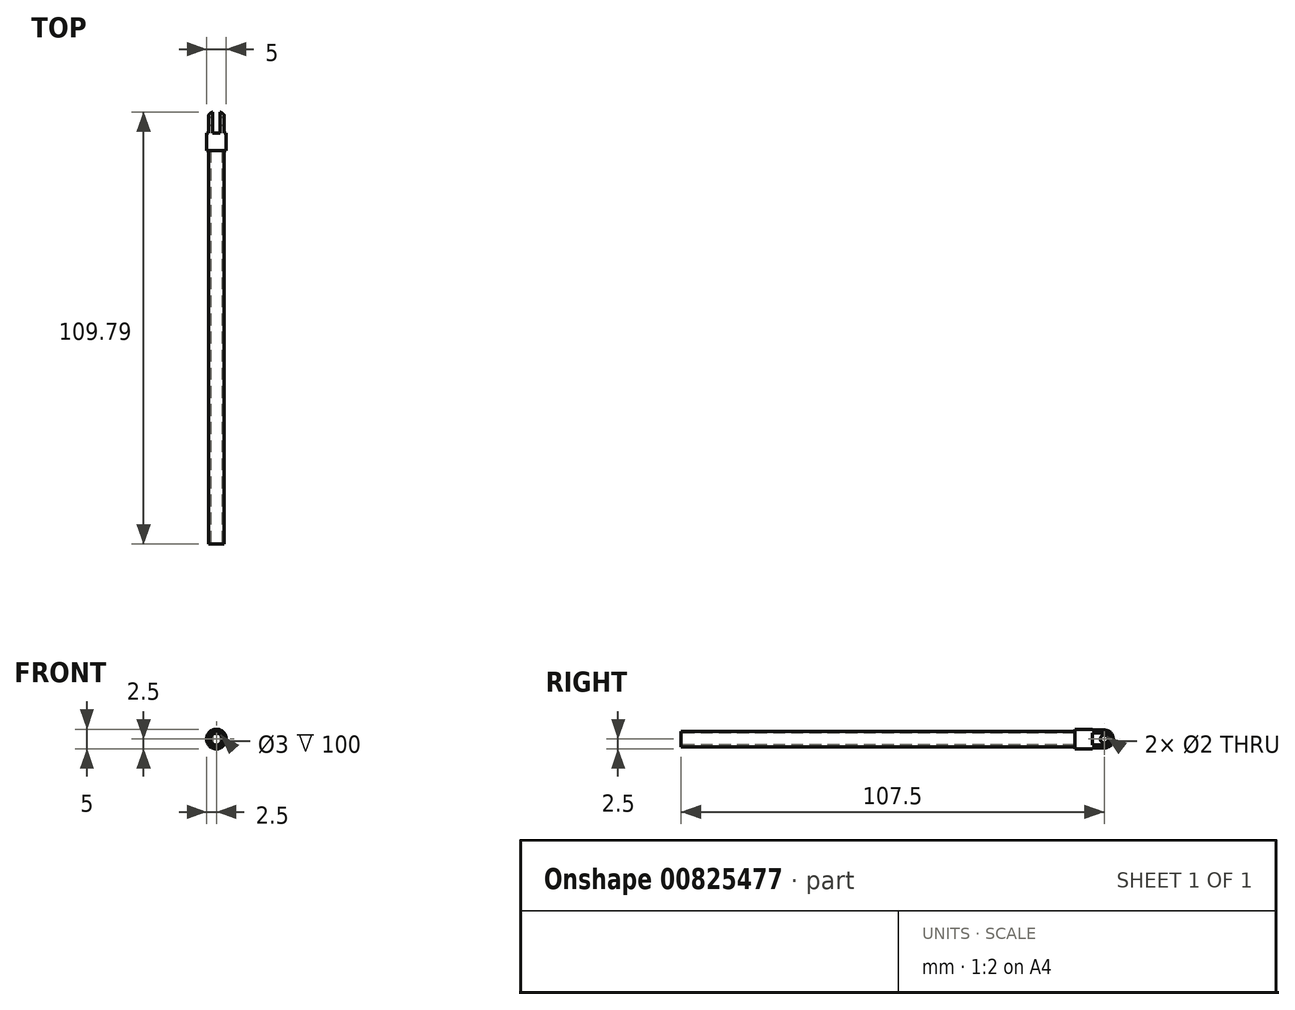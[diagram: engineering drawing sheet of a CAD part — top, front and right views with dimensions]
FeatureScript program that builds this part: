
annotation { "Feature Type Name" : "Feature", "Feature Type Description" : "" }
export const myFeature = defineFeature(function(context is Context, id is Id, definition is map)
    precondition{}
    {
        {
            var Q0;
            Q0=qCreatedBy(makeId("Front.planeOp"),FACE);
            var sketch = newSketch(context, id + "F0", { "sketchPlane" : qUnion([Q0])});
            skCircle(sketch, "E0", {"center": v(0, 0) * mm, "radius": 2 * mm});
            skSolve(sketch);
        }
        {
            var Q0;
            Q0 = qSketchRegion(id + "F0", true);
            extrude(context, id + "F1", {"entities" : qUnion([Q0]), "endBound" : BoundingType.SYMMETRIC, "depth" : 100 * mm, "offsetDistance" : 25 * mm});
        }
        {
            var Q0;
            Q0=makeQuery(id+"F1.opExtrude","CAP_FACE",FACE,{"disambiguationData":[OSD([sQuery(id+"F0.wireOp",EDGE,"E0")])],"isStart":true});
            var sketch = newSketch(context, id + "F2", { "sketchPlane" : qUnion([Q0])});
            skCircle(sketch, "E1", {"center": v(0, 0) * mm, "radius": 2.5 * mm});
            skSolve(sketch);
        }
        {
            var Q0;
            Q0 = qSketchRegion(id + "F2", true);
            extrude(context, id + "F3", {"entities" : qUnion([Q0]), "operationType" : NewBodyOperationType.ADD, "depth" : 10 * mm, "offsetDistance" : 25 * mm});
        }
        {
            var Q0;
            Q0=makeQuery(id+"F3.opExtrude","CAP_EDGE",EDGE,{"disambiguationData":[OSD([sQuery(id+"F2.wireOp",EDGE,"E1")])],"isStart":false});
            fillet(context, id + "F4", {"entities" : qUnion([Q0]), "radius" : 2.5 * mm, "tangentPropagation" : true, "allowEdgeOverflow" : false});
        }
        {
            var Q0;
            Q0=qCreatedBy(makeId("Top.planeOp"),FACE);
            var sketch = newSketch(context, id + "F5", { "sketchPlane" : qUnion([Q0])});
            skLineSegment(sketch, "E2.bottom", {"start": v(1, 54.5) * mm, "end": v(-1, 54.5) * mm});
            skLineSegment(sketch, "E2.top", {"start": v(1, 60.5) * mm, "end": v(-1, 60.5) * mm});
            skLineSegment(sketch, "E2.left", {"start": v(1, 54.5) * mm, "end": v(1, 60.5) * mm});
            skLineSegment(sketch, "E2.right", {"start": v(-1, 54.5) * mm, "end": v(-1, 60.5) * mm});
            skPoint(sketch, "E2.middle", {"position": v(0, 57.5) * mm});
            skLineSegment(sketch, "E3", {"start": v(-1, 54.5) * mm, "end": v(-2, 54.5) * mm, "construction": true});
            skLineSegment(sketch, "E4", {"start": v(1, 54.5) * mm, "end": v(2, 54.5) * mm, "construction": true});
            skLineSegment(sketch, "E5.bottom", {"start": v(-2, 54.5) * mm, "end": v(-3.04, 54.5) * mm});
            skLineSegment(sketch, "E5.top", {"start": v(-2, 60.52) * mm, "end": v(-3.04, 60.52) * mm});
            skLineSegment(sketch, "E5.left", {"start": v(-2, 54.5) * mm, "end": v(-2, 60.52) * mm});
            skLineSegment(sketch, "E5.right", {"start": v(-3.04, 54.5) * mm, "end": v(-3.04, 60.52) * mm});
            skLineSegment(sketch, "E6.bottom", {"start": v(2, 54.5) * mm, "end": v(3.05, 54.5) * mm});
            skLineSegment(sketch, "E6.top", {"start": v(2, 60.56) * mm, "end": v(3.05, 60.56) * mm});
            skLineSegment(sketch, "E6.left", {"start": v(2, 54.5) * mm, "end": v(2, 60.56) * mm});
            skLineSegment(sketch, "E6.right", {"start": v(3.05, 54.5) * mm, "end": v(3.05, 60.56) * mm});
            skSolve(sketch);
        }
        {
            var Q0;
            Q0=makeQuery(id+"F5.imprint","IMPRINT",FACE,{"disambiguationData":[TD([[makeQuery(id+"F5.imprint","IMPRINT",EDGE,{"derivedFrom":sQuery(id+"F5.wireOp",EDGE,"E2.bottom")}),-1.0]])]});
            var Q1;
            Q1=makeQuery(id+"F5.imprint","IMPRINT",FACE,{"disambiguationData":[TD([[makeQuery(id+"F5.imprint","IMPRINT",EDGE,{"derivedFrom":sQuery(id+"F5.wireOp",EDGE,"E5.bottom")}),-1.0]])]});
            var Q2;
            Q2=makeQuery(id+"F5.imprint","IMPRINT",FACE,{"disambiguationData":[TD([[makeQuery(id+"F5.imprint","IMPRINT",EDGE,{"derivedFrom":sQuery(id+"F5.wireOp",EDGE,"E6.bottom")}),1.0]])]});
            extrude(context, id + "F6", {"entities" : qUnion([Q0, Q1, Q2]), "operationType" : NewBodyOperationType.REMOVE, "endBound" : BoundingType.SYMMETRIC, "depth" : 25 * mm, "offsetDistance" : 25 * mm});
        }
        {
            var Q0;
            Q0=makeQuery(id+"F6.boolean.opBoolean","COPY",FACE,{"derivedFrom":makeQuery(id+"F6.opExtrude","SWEPT_FACE",FACE,{"disambiguationData":[OSD([sQuery(id+"F5.wireOp",EDGE,"E6.left")])]})});
            var sketch = newSketch(context, id + "F7", { "sketchPlane" : qUnion([Q0])});
            skCircle(sketch, "E7", {"center": v(57.5, 0) * mm, "radius": 1 * mm});
            skSolve(sketch);
        }
        {
            var Q0;
            Q0 = qSketchRegion(id + "F7", true);
            extrude(context, id + "F8", {"entities" : qUnion([Q0]), "operationType" : NewBodyOperationType.REMOVE, "oppositeDirection" : true, "depth" : 4.7 * mm, "offsetDistance" : 25 * mm});
        }
        {
            var Q0;
            Q0=makeQuery(id+"F1.opExtrude","CAP_FACE",FACE,{"disambiguationData":[OSD([sQuery(id+"F0.wireOp",EDGE,"E0")])],"isStart":false});
            var sketch = newSketch(context, id + "F9", { "sketchPlane" : qUnion([Q0])});
            skCircle(sketch, "E8", {"center": v(0, 0) * mm, "radius": 1.5 * mm});
            skSolve(sketch);
        }
        {
            var Q0;
            Q0 = qSketchRegion(id + "F9", true);
            extrude(context, id + "F10", {"entities" : qUnion([Q0]), "operationType" : NewBodyOperationType.REMOVE, "oppositeDirection" : true, "depth" : 100 * mm, "offsetDistance" : 25 * mm});
        }
    });
